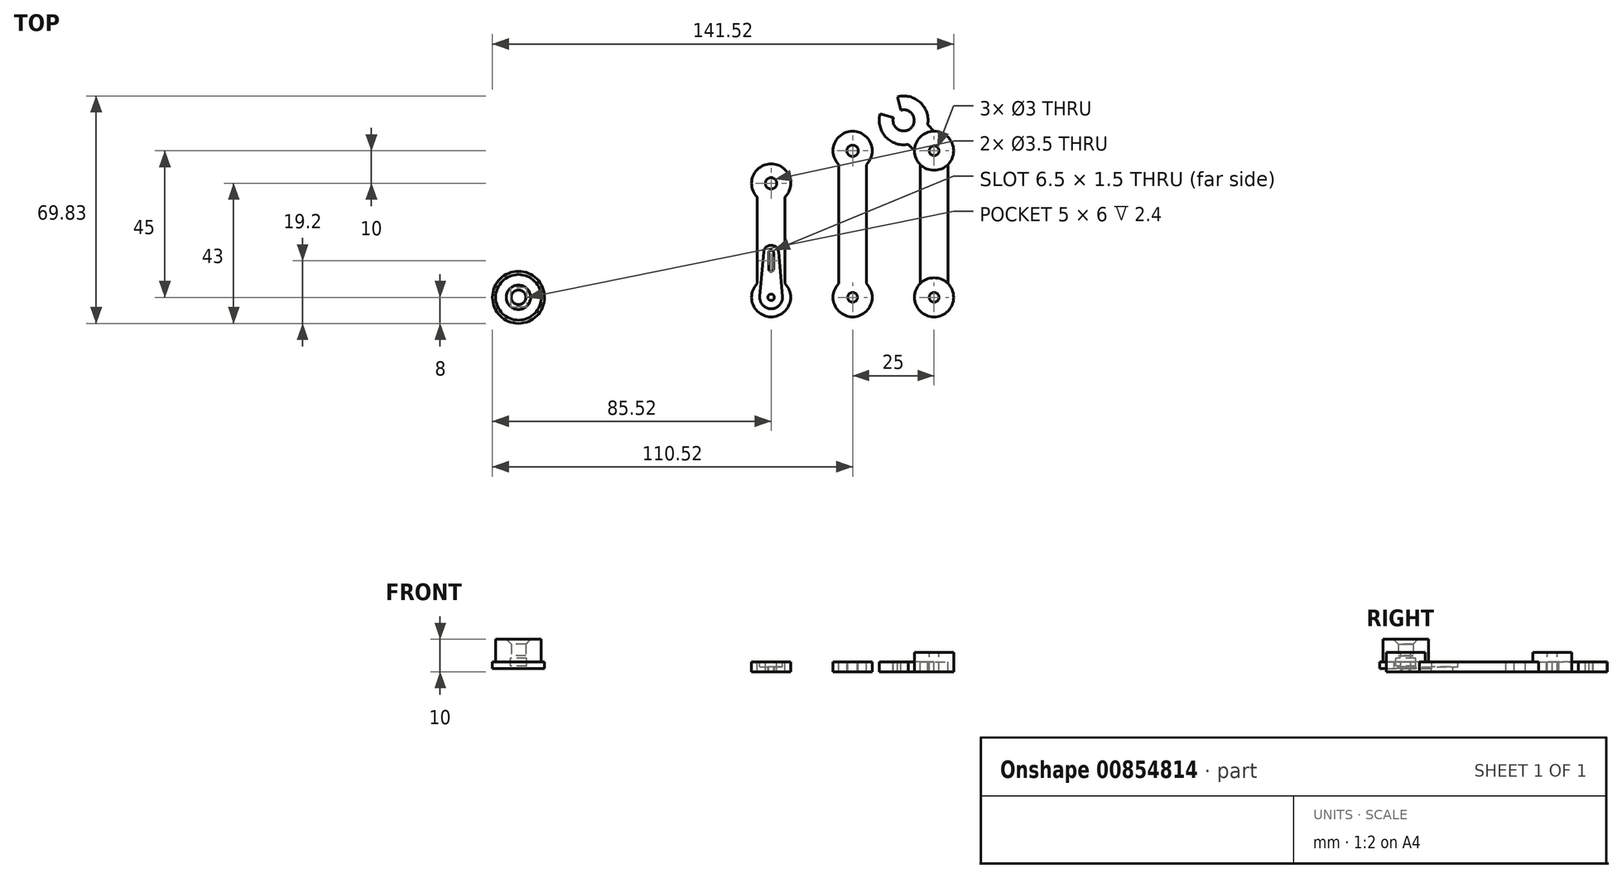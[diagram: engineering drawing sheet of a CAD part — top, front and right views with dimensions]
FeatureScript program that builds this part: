
annotation { "Feature Type Name" : "Feature", "Feature Type Description" : "" }
export const myFeature = defineFeature(function(context is Context, id is Id, definition is map)
    precondition{}
    {
        {
            var Q0;
            Q0=qCreatedBy(makeId("Top.planeOp"),FACE);
            var sketch = newSketch(context, id + "F0", { "sketchPlane" : qUnion([Q0])});
            skCircle(sketch, "E0", {"center": v(0, 0) * mm, "radius": 6 * mm});
            skCircle(sketch, "E1", {"center": v(0, 0) * mm, "radius": 3.5 * mm});
            skCircle(sketch, "E2", {"center": v(0, 0) * mm, "radius": 1 * mm});
            skLineSegment(sketch, "E3", {"start": v(0, -6) * mm, "end": v(0, 41) * mm, "construction": true});
            skCircle(sketch, "E4", {"center": v(0, 35) * mm, "radius": 1.75 * mm});
            skCircle(sketch, "E5", {"center": v(0, 35) * mm, "radius": 6 * mm});
            skLineSegment(sketch, "E6", {"start": v(4.25, 4.24) * mm, "end": v(4.25, 30.76) * mm});
            skLineSegment(sketch, "E7.MirrorCS", {"start": v(-4.25, 4.24) * mm, "end": v(-4.25, 30.76) * mm});
            skCircle(sketch, "E8", {"center": v(0, 13.7) * mm, "radius": 2.3 * mm});
            skPoint(sketch, "E9", {"position": v(0, 16) * mm});
            skPoint(sketch, "E10", {"position": v(0, -3.5) * mm});
            skLineSegment(sketch, "E11", {"start": v(3.49, 0.3) * mm, "end": v(2.3, 13.9) * mm});
            skLineSegment(sketch, "E12.MirrorCS", {"start": v(-3.49, 0.3) * mm, "end": v(-2.3, 13.9) * mm});
            skCircle(sketch, "E13", {"center": v(25, 0) * mm, "radius": 6 * mm});
            skCircle(sketch, "E14", {"center": v(25, 0) * mm, "radius": 1.5 * mm});
            skLineSegment(sketch, "E15", {"start": v(25, -6) * mm, "end": v(25, 51) * mm, "construction": true});
            skCircle(sketch, "E16", {"center": v(25, 45) * mm, "radius": 1.75 * mm});
            skCircle(sketch, "E17", {"center": v(25, 45) * mm, "radius": 6 * mm});
            skLineSegment(sketch, "E18", {"start": v(29.25, 4.24) * mm, "end": v(29.25, 40.76) * mm});
            skLineSegment(sketch, "E19.MirrorCS", {"start": v(20.75, 4.24) * mm, "end": v(20.75, 40.76) * mm});
            skCircle(sketch, "E20", {"center": v(50, 0) * mm, "radius": 6 * mm});
            skCircle(sketch, "E21", {"center": v(50, 0) * mm, "radius": 1.5 * mm});
            skLineSegment(sketch, "E22", {"start": v(50, -6) * mm, "end": v(50, 51) * mm, "construction": true});
            skCircle(sketch, "E23", {"center": v(50, 45) * mm, "radius": 1.5 * mm});
            skCircle(sketch, "E24", {"center": v(50, 45) * mm, "radius": 6 * mm});
            skLineSegment(sketch, "E25", {"start": v(54.25, 4.24) * mm, "end": v(54.25, 40.76) * mm});
            skLineSegment(sketch, "E26.MirrorCS", {"start": v(45.75, 4.24) * mm, "end": v(45.75, 40.76) * mm});
            skLineSegment(sketch, "E27", {"start": v(50, 45) * mm, "end": v(35.36, 59.64) * mm, "construction": true});
            skCircle(sketch, "E28", {"center": v(40.67, 54.33) * mm, "radius": 7.5 * mm});
            skCircle(sketch, "E29", {"center": v(40.67, 54.33) * mm, "radius": 3.25 * mm});
            skLineSegment(sketch, "E30", {"start": v(42.03, 46.96) * mm, "end": v(44, 44.99) * mm});
            skLineSegment(sketch, "E31.MirrorCS", {"start": v(48.04, 52.97) * mm, "end": v(50.01, 51) * mm});
            skLineSegment(sketch, "E32", {"start": v(45.75, 22.5) * mm, "end": v(54.25, 22.5) * mm, "construction": true});
            skLineSegment(sketch, "E33", {"start": v(20.75, 22.5) * mm, "end": v(29.25, 22.5) * mm, "construction": true});
            skLineSegment(sketch, "E34", {"start": v(-4.25, 17.5) * mm, "end": v(4.25, 17.5) * mm, "construction": true});
            skLineSegment(sketch, "E35", {"start": v(43.02, 45.97) * mm, "end": v(49.03, 51.98) * mm, "construction": true});
            skLineSegment(sketch, "E36", {"start": v(37.53, 55.17) * mm, "end": v(33.42, 56.27) * mm});
            skLineSegment(sketch, "E37.MirrorCS", {"start": v(39.83, 57.47) * mm, "end": v(38.73, 61.58) * mm});
            skCircle(sketch, "E38", {"center": v(-77.52, 0) * mm, "radius": 8 * mm});
            skCircle(sketch, "E39", {"center": v(-77.52, 0) * mm, "radius": 7 * mm});
            skCircle(sketch, "E40", {"center": v(-77.52, 0) * mm, "radius": 3.3 * mm});
            skCircle(sketch, "E41", {"center": v(-77.52, 0) * mm, "radius": 2.25 * mm});
            skLineSegment(sketch, "E42", {"start": v(0, 13.7) * mm, "end": v(0, 8.7) * mm});
            skArc(sketch, "E43.0.startCap", {"start": v(-0.75, 13.7) * mm, "mid": v(0, 14.45) * mm, "end": v(0.75, 13.7) * mm});
            skArc(sketch, "E43.0.endCap", {"start": v(0.75, 8.7) * mm, "mid": v(0, 7.95) * mm, "end": v(-0.75, 8.7) * mm});
            skLineSegment(sketch, "E43.0.left", {"start": v(0.75, 13.7) * mm, "end": v(0.75, 8.7) * mm});
            skLineSegment(sketch, "E43.0.right", {"start": v(-0.75, 13.7) * mm, "end": v(-0.75, 8.7) * mm});
            skSolve(sketch);
        }
        {
            var Q0;
            {var subQ0=sQuery(id+"F0.wireOp",EDGE,"E6");Q0=makeQuery(id+"F0.imprint","IMPRINT",FACE,{"disambiguationData":[TD([[makeQuery(id+"F0.imprint","IMPRINT",EDGE,{"derivedFrom":subQ0}),1.0]])]});}
            var Q1;
            Q1=makeQuery(id+"F0.imprint","IMPRINT",FACE,{"disambiguationData":[TD([[makeQuery(id+"F0.imprint","IMPRINT",EDGE,{"derivedFrom":sQuery(id+"F0.wireOp",EDGE,"E4")}),-1.0]])]});
            var Q2;
            {var subQ0=sQuery(id+"F0.wireOp",EDGE,"E8");var subQ1=makeQuery(id+"F0.imprint","INTERSECT",VERTEX,{"derivedFrom":[subQ0,sQuery(id+"F0.wireOp",EDGE,"E11")]});Q2=makeQuery(id+"F0.imprint","IMPRINT",FACE,{"disambiguationData":[TD([[makeQuery(id+"F0.imprint","IMPRINT",EDGE,{"disambiguationData":[TD([[subQ1,-1.0]])],"derivedFrom":subQ0}),1.0]])]});}
            var Q3;
            {var subQ0=sQuery(id+"F0.wireOp",EDGE,"E11");var subQ1=sQuery(id+"F0.wireOp",EDGE,"E0");var subQ2=makeQuery(id+"F0.imprint","INTERSECT",VERTEX,{"derivedFrom":[subQ1,subQ0]});Q3=makeQuery(id+"F0.imprint","IMPRINT",FACE,{"disambiguationData":[TD([[makeQuery(id+"F0.imprint","IMPRINT",EDGE,{"disambiguationData":[TD([[subQ2,-1.0]])],"derivedFrom":subQ1}),-1.0]])]});}
            var Q4;
            {var subQ0=sQuery(id+"F0.wireOp",EDGE,"E11");var subQ1=sQuery(id+"F0.wireOp",EDGE,"E0");var subQ2=makeQuery(id+"F0.imprint","INTERSECT",VERTEX,{"derivedFrom":[subQ1,subQ0]});Q4=makeQuery(id+"F0.imprint","IMPRINT",FACE,{"disambiguationData":[TD([[makeQuery(id+"F0.imprint","IMPRINT",EDGE,{"disambiguationData":[TD([[subQ2,-1.0]])],"derivedFrom":subQ1}),1.0]])]});}
            var Q5;
            {var subQ0=sQuery(id+"F0.wireOp",EDGE,"E0");var subQ1=makeQuery(id+"F0.imprint","INTERSECT",VERTEX,{"derivedFrom":[subQ0,sQuery(id+"F0.wireOp",EDGE,"E6")]});Q5=makeQuery(id+"F0.imprint","IMPRINT",FACE,{"disambiguationData":[TD([[makeQuery(id+"F0.imprint","IMPRINT",EDGE,{"disambiguationData":[TD([[subQ1,-1.0]])],"derivedFrom":subQ0}),1.0]])]});}
            var Q6;
            Q6=makeQuery(id+"F0.imprint","IMPRINT",FACE,{"disambiguationData":[TD([[makeQuery(id+"F0.imprint","IMPRINT",EDGE,{"derivedFrom":sQuery(id+"F0.wireOp",EDGE,"E2")}),-1.0]])]});
            var Q7;
            Q7=makeQuery(id+"F0.imprint","IMPRINT",FACE,{"disambiguationData":[TD([[makeQuery(id+"F0.imprint","IMPRINT",EDGE,{"derivedFrom":sQuery(id+"F0.wireOp",EDGE,"E16")}),-1.0]])]});
            var Q8;
            {var subQ0=sQuery(id+"F0.wireOp",EDGE,"E18");Q8=makeQuery(id+"F0.imprint","IMPRINT",FACE,{"disambiguationData":[TD([[makeQuery(id+"F0.imprint","IMPRINT",EDGE,{"derivedFrom":subQ0}),1.0]])]});}
            var Q9;
            Q9=makeQuery(id+"F0.imprint","IMPRINT",FACE,{"disambiguationData":[TD([[makeQuery(id+"F0.imprint","IMPRINT",EDGE,{"derivedFrom":sQuery(id+"F0.wireOp",EDGE,"E14")}),-1.0]])]});
            var Q10;
            Q10=makeQuery(id+"F0.imprint","IMPRINT",FACE,{"disambiguationData":[TD([[makeQuery(id+"F0.imprint","IMPRINT",EDGE,{"derivedFrom":sQuery(id+"F0.wireOp",EDGE,"E23")}),-1.0]])]});
            var Q11;
            {var subQ0=sQuery(id+"F0.wireOp",EDGE,"E30");Q11=makeQuery(id+"F0.imprint","IMPRINT",FACE,{"disambiguationData":[TD([[makeQuery(id+"F0.imprint","IMPRINT",EDGE,{"derivedFrom":subQ0}),1.0]])]});}
            var Q12;
            {var subQ0=sQuery(id+"F0.wireOp",EDGE,"E31.MirrorCS");Q12=makeQuery(id+"F0.imprint","IMPRINT",FACE,{"disambiguationData":[TD([[makeQuery(id+"F0.imprint","IMPRINT",EDGE,{"derivedFrom":subQ0}),-1.0]])]});}
            var Q13;
            {var subQ0=sQuery(id+"F0.wireOp",EDGE,"E28");var subQ1=sQuery(id+"F0.wireOp",EDGE,"E24");var subQ2=makeQuery(id+"F0.imprint","INTERSECT",VERTEX,{"disambiguationData":[OD(0.0)],"derivedFrom":[subQ1,subQ0]});Q13=makeQuery(id+"F0.imprint","IMPRINT",FACE,{"disambiguationData":[TD([[makeQuery(id+"F0.imprint","IMPRINT",EDGE,{"disambiguationData":[TD([[subQ2,-1.0]])],"derivedFrom":subQ1}),1.0]])]});}
            var Q14;
            {var subQ0=sQuery(id+"F0.wireOp",EDGE,"E25");Q14=makeQuery(id+"F0.imprint","IMPRINT",FACE,{"disambiguationData":[TD([[makeQuery(id+"F0.imprint","IMPRINT",EDGE,{"derivedFrom":subQ0}),1.0]])]});}
            var Q15;
            Q15=makeQuery(id+"F0.imprint","IMPRINT",FACE,{"disambiguationData":[TD([[makeQuery(id+"F0.imprint","IMPRINT",EDGE,{"derivedFrom":sQuery(id+"F0.wireOp",EDGE,"E21")}),-1.0]])]});
            var Q16;
            {var subQ6=sQuery(id+"F0.wireOp",EDGE,"E36");Q16=makeQuery(id+"F0.imprint","IMPRINT",FACE,{"disambiguationData":[TD([[makeQuery(id+"F0.imprint","IMPRINT",EDGE,{"derivedFrom":subQ6}),1.0]])]});}
            extrude(context, id + "F1", {"entities" : qUnion([Q0, Q1, Q2, Q3, Q4, Q5, Q6, Q7, Q8, Q9, Q10, Q11, Q12, Q13, Q14, Q15, Q16]), "oppositeDirection" : true, "depth" : 3 * mm, "offsetDistance" : 25 * mm});
        }
        {
            var Q0;
            {var subQ0=sQuery(id+"F0.wireOp",EDGE,"E8");var subQ1=makeQuery(id+"F0.imprint","INTERSECT",VERTEX,{"derivedFrom":[subQ0,sQuery(id+"F0.wireOp",EDGE,"E11")]});Q0=makeQuery(id+"F0.imprint","IMPRINT",FACE,{"disambiguationData":[TD([[makeQuery(id+"F0.imprint","IMPRINT",EDGE,{"disambiguationData":[TD([[subQ1,-1.0]])],"derivedFrom":subQ0}),1.0]])]});}
            var Q1;
            {var subQ0=sQuery(id+"F0.wireOp",EDGE,"E11");var subQ1=sQuery(id+"F0.wireOp",EDGE,"E0");var subQ2=makeQuery(id+"F0.imprint","INTERSECT",VERTEX,{"derivedFrom":[subQ1,subQ0]});Q1=makeQuery(id+"F0.imprint","IMPRINT",FACE,{"disambiguationData":[TD([[makeQuery(id+"F0.imprint","IMPRINT",EDGE,{"disambiguationData":[TD([[subQ2,-1.0]])],"derivedFrom":subQ1}),-1.0]])]});}
            var Q2;
            {var subQ0=sQuery(id+"F0.wireOp",EDGE,"E11");var subQ1=sQuery(id+"F0.wireOp",EDGE,"E0");var subQ2=makeQuery(id+"F0.imprint","INTERSECT",VERTEX,{"derivedFrom":[subQ1,subQ0]});Q2=makeQuery(id+"F0.imprint","IMPRINT",FACE,{"disambiguationData":[TD([[makeQuery(id+"F0.imprint","IMPRINT",EDGE,{"disambiguationData":[TD([[subQ2,-1.0]])],"derivedFrom":subQ1}),1.0]])]});}
            var Q3;
            Q3=makeQuery(id+"F0.imprint","IMPRINT",FACE,{"disambiguationData":[TD([[makeQuery(id+"F0.imprint","IMPRINT",EDGE,{"derivedFrom":sQuery(id+"F0.wireOp",EDGE,"E2")}),-1.0]])]});
            extrude(context, id + "F2", {"entities" : qUnion([Q0, Q1, Q2, Q3]), "operationType" : NewBodyOperationType.REMOVE, "oppositeDirection" : true, "depth" : 1.5 * mm, "offsetDistance" : 25 * mm});
        }
        {
            var Q0;
            Q0=makeQuery(id+"F0.imprint","IMPRINT",FACE,{"disambiguationData":[TD([[makeQuery(id+"F0.imprint","IMPRINT",EDGE,{"derivedFrom":sQuery(id+"F0.wireOp",EDGE,"E23")}),-1.0]])]});
            var Q1;
            {var subQ0=sQuery(id+"F0.wireOp",EDGE,"E28");var subQ1=sQuery(id+"F0.wireOp",EDGE,"E24");var subQ2=makeQuery(id+"F0.imprint","INTERSECT",VERTEX,{"disambiguationData":[OD(0.0)],"derivedFrom":[subQ1,subQ0]});Q1=makeQuery(id+"F0.imprint","IMPRINT",FACE,{"disambiguationData":[TD([[makeQuery(id+"F0.imprint","IMPRINT",EDGE,{"disambiguationData":[TD([[subQ2,-1.0]])],"derivedFrom":subQ1}),1.0]])]});}
            var Q2;
            Q2=makeQuery(id+"F0.imprint","IMPRINT",FACE,{"disambiguationData":[TD([[makeQuery(id+"F0.imprint","IMPRINT",EDGE,{"derivedFrom":sQuery(id+"F0.wireOp",EDGE,"E21")}),-1.0]])]});
            extrude(context, id + "F3", {"entities" : qUnion([Q0, Q1, Q2]), "operationType" : NewBodyOperationType.ADD, "depth" : 3 * mm, "offsetDistance" : 25 * mm});
        }
        {
            var Q0;
            Q0=makeQuery(id+"F0.imprint","IMPRINT",FACE,{"disambiguationData":[TD([[makeQuery(id+"F0.imprint","IMPRINT",EDGE,{"derivedFrom":sQuery(id+"F0.wireOp",EDGE,"E38")}),1.0]])]});
            var Q1;
            Q1=makeQuery(id+"F0.imprint","IMPRINT",FACE,{"disambiguationData":[TD([[makeQuery(id+"F0.imprint","IMPRINT",EDGE,{"derivedFrom":sQuery(id+"F0.wireOp",EDGE,"U8XN3V2j-0AhI-ton1-zM9Y-7LPwTmasrNIo.bottom")}),1.0]])]});
            var Q2;
            {var subQ0=sQuery(id+"F0.wireOp",EDGE,"U8XN3V2j-0AhI-ton1-zM9Y-7LPwTmasrNIo.right");var subQ1=sQuery(id+"F0.wireOp",EDGE,"E40");var subQ2=makeQuery(id+"F0.imprint","INTERSECT",VERTEX,{"disambiguationData":[OD(0.0)],"derivedFrom":[subQ1,subQ0]});Q2=makeQuery(id+"F0.imprint","IMPRINT",FACE,{"disambiguationData":[TD([[makeQuery(id+"F0.imprint","IMPRINT",EDGE,{"disambiguationData":[TD([[subQ2,-1.0]])],"derivedFrom":subQ1}),1.0]])]});}
            var Q3;
            Q3=makeQuery(id+"F0.imprint","IMPRINT",FACE,{"disambiguationData":[TD([[makeQuery(id+"F0.imprint","IMPRINT",EDGE,{"derivedFrom":sQuery(id+"F0.wireOp",EDGE,"E39")}),1.0]])]});
            var Q4;
            Q4=makeQuery(id+"F0.imprint","IMPRINT",FACE,{"disambiguationData":[TD([[makeQuery(id+"F0.imprint","IMPRINT",EDGE,{"derivedFrom":sQuery(id+"F0.wireOp",EDGE,"E41")}),1.0]])]});
            var Q5;
            {var subQ0=sQuery(id+"F0.wireOp",EDGE,"U8XN3V2j-0AhI-ton1-zM9Y-7LPwTmasrNIo.left");var subQ1=sQuery(id+"F0.wireOp",EDGE,"E40");var subQ2=makeQuery(id+"F0.imprint","INTERSECT",VERTEX,{"disambiguationData":[OD(0.0)],"derivedFrom":[subQ1,subQ0]});Q5=makeQuery(id+"F0.imprint","IMPRINT",FACE,{"disambiguationData":[TD([[makeQuery(id+"F0.imprint","IMPRINT",EDGE,{"disambiguationData":[TD([[subQ2,1.0]])],"derivedFrom":subQ1}),1.0]])]});}
            var Q6;
            Q6=makeQuery(id+"F0.imprint","IMPRINT",FACE,{"disambiguationData":[TD([[makeQuery(id+"F0.imprint","IMPRINT",EDGE,{"derivedFrom":sQuery(id+"F0.wireOp",EDGE,"E41")}),-1.0]])]});
            var Q7;
            {var subQ0=sQuery(id+"F0.wireOp",EDGE,"U8XN3V2j-0AhI-ton1-zM9Y-7LPwTmasrNIo.top");var subQ1=sQuery(id+"F0.wireOp",EDGE,"E40");var subQ2=makeQuery(id+"F0.imprint","INTERSECT",VERTEX,{"disambiguationData":[OD(0.0)],"derivedFrom":[subQ1,subQ0]});Q7=makeQuery(id+"F0.imprint","IMPRINT",FACE,{"disambiguationData":[TD([[makeQuery(id+"F0.imprint","IMPRINT",EDGE,{"disambiguationData":[TD([[subQ2,-1.0]])],"derivedFrom":subQ1}),1.0]])]});}
            var Q8;
            {var subQ0=sQuery(id+"F0.wireOp",EDGE,"U8XN3V2j-0AhI-ton1-zM9Y-7LPwTmasrNIo.right");var subQ1=sQuery(id+"F0.wireOp",EDGE,"E40");var subQ2=makeQuery(id+"F0.imprint","INTERSECT",VERTEX,{"disambiguationData":[OD(1.0)],"derivedFrom":[subQ1,subQ0]});Q8=makeQuery(id+"F0.imprint","IMPRINT",FACE,{"disambiguationData":[TD([[makeQuery(id+"F0.imprint","IMPRINT",EDGE,{"disambiguationData":[TD([[subQ2,-1.0]])],"derivedFrom":subQ1}),-1.0]])]});}
            var Q9;
            {var subQ0=sQuery(id+"F0.wireOp",EDGE,"U8XN3V2j-0AhI-ton1-zM9Y-7LPwTmasrNIo.top");var subQ1=sQuery(id+"F0.wireOp",EDGE,"E40");var subQ2=makeQuery(id+"F0.imprint","INTERSECT",VERTEX,{"disambiguationData":[OD(1.0)],"derivedFrom":[subQ1,subQ0]});Q9=makeQuery(id+"F0.imprint","IMPRINT",FACE,{"disambiguationData":[TD([[makeQuery(id+"F0.imprint","IMPRINT",EDGE,{"disambiguationData":[TD([[subQ2,-1.0]])],"derivedFrom":subQ1}),-1.0]])]});}
            var Q10;
            {var subQ0=sQuery(id+"F0.wireOp",EDGE,"U8XN3V2j-0AhI-ton1-zM9Y-7LPwTmasrNIo.bottom");var subQ1=sQuery(id+"F0.wireOp",EDGE,"E40");var subQ2=makeQuery(id+"F0.imprint","INTERSECT",VERTEX,{"disambiguationData":[OD(0.0)],"derivedFrom":[subQ1,subQ0]});Q10=makeQuery(id+"F0.imprint","IMPRINT",FACE,{"disambiguationData":[TD([[makeQuery(id+"F0.imprint","IMPRINT",EDGE,{"disambiguationData":[TD([[subQ2,-1.0]])],"derivedFrom":subQ1}),1.0]])]});}
            extrude(context, id + "F4", {"entities" : qUnion([Q0, Q1, Q2, Q3, Q4, Q5, Q6, Q7, Q8, Q9, Q10]), "oppositeDirection" : true, "depth" : 2 * mm, "offsetDistance" : 25 * mm});
        }
        {
            var Q0;
            Q0=makeQuery(id+"F0.imprint","IMPRINT",FACE,{"disambiguationData":[TD([[makeQuery(id+"F0.imprint","IMPRINT",EDGE,{"derivedFrom":sQuery(id+"F0.wireOp",EDGE,"U8XN3V2j-0AhI-ton1-zM9Y-7LPwTmasrNIo.bottom")}),1.0]])]});
            var Q1;
            Q1=makeQuery(id+"F0.imprint","IMPRINT",FACE,{"disambiguationData":[TD([[makeQuery(id+"F0.imprint","IMPRINT",EDGE,{"derivedFrom":sQuery(id+"F0.wireOp",EDGE,"E41")}),1.0]])]});
            extrude(context, id + "F5", {"entities" : qUnion([Q0, Q1]), "operationType" : NewBodyOperationType.ADD, "depth" : 2 * mm, "offsetDistance" : 25 * mm});
        }
        {
            var Q0;
            Q0=makeQuery(id+"F0.imprint","IMPRINT",FACE,{"disambiguationData":[TD([[makeQuery(id+"F0.imprint","IMPRINT",EDGE,{"derivedFrom":sQuery(id+"F0.wireOp",EDGE,"E39")}),1.0]])]});
            var Q1;
            Q1=makeQuery(id+"F0.imprint","IMPRINT",FACE,{"disambiguationData":[TD([[makeQuery(id+"F0.imprint","IMPRINT",EDGE,{"derivedFrom":sQuery(id+"F0.wireOp",EDGE,"E40")}),1.0]])]});
            extrude(context, id + "F6", {"entities" : qUnion([Q0, Q1]), "operationType" : NewBodyOperationType.ADD, "depth" : 7 * mm, "offsetDistance" : 25 * mm});
        }
        {
            var Q0;
            Q0=makeQuery(id+"F0.imprint","IMPRINT",FACE,{"disambiguationData":[TD([[makeQuery(id+"F0.imprint","IMPRINT",EDGE,{"derivedFrom":sQuery(id+"F0.wireOp",EDGE,"E41")}),1.0]])]});
            var sketch = newSketch(context, id + "F7", { "sketchPlane" : qUnion([Q0])});
            skLineSegment(sketch, "E44.bottom", {"start": v(-75.02, 3) * mm, "end": v(-80.02, 3) * mm});
            skLineSegment(sketch, "E44.top", {"start": v(-75.02, -3) * mm, "end": v(-80.02, -3) * mm});
            skLineSegment(sketch, "E44.left", {"start": v(-75.02, 3) * mm, "end": v(-75.02, -3) * mm});
            skLineSegment(sketch, "E44.right", {"start": v(-80.02, 3) * mm, "end": v(-80.02, -3) * mm});
            skLineSegment(sketch, "E45", {"start": v(-75.02, -3) * mm, "end": v(-80.02, 3) * mm, "construction": true});
            skSolve(sketch);
        }
        {
            var Q0;
            Q0 = qSketchRegion(id + "F7", true);
            extrude(context, id + "F8", {"entities" : qUnion([Q0]), "operationType" : NewBodyOperationType.REMOVE, "endBound" : BoundingType.SYMMETRIC, "oppositeDirection" : true, "depth" : 2.4 * mm, "offsetDistance" : 25 * mm});
        }
        {
            var Q0;
            Q0=makeQuery(id+"F6.opExtrude","CAP_EDGE",EDGE,{"disambiguationData":[OSD([sQuery(id+"F0.wireOp",EDGE,"E41")])],"isStart":false});
            chamfer(context, id + "F9", {"entities" : qUnion([Q0]), "width" : 1.5 * mm, "tangentPropagation" : true});
        }
    });
